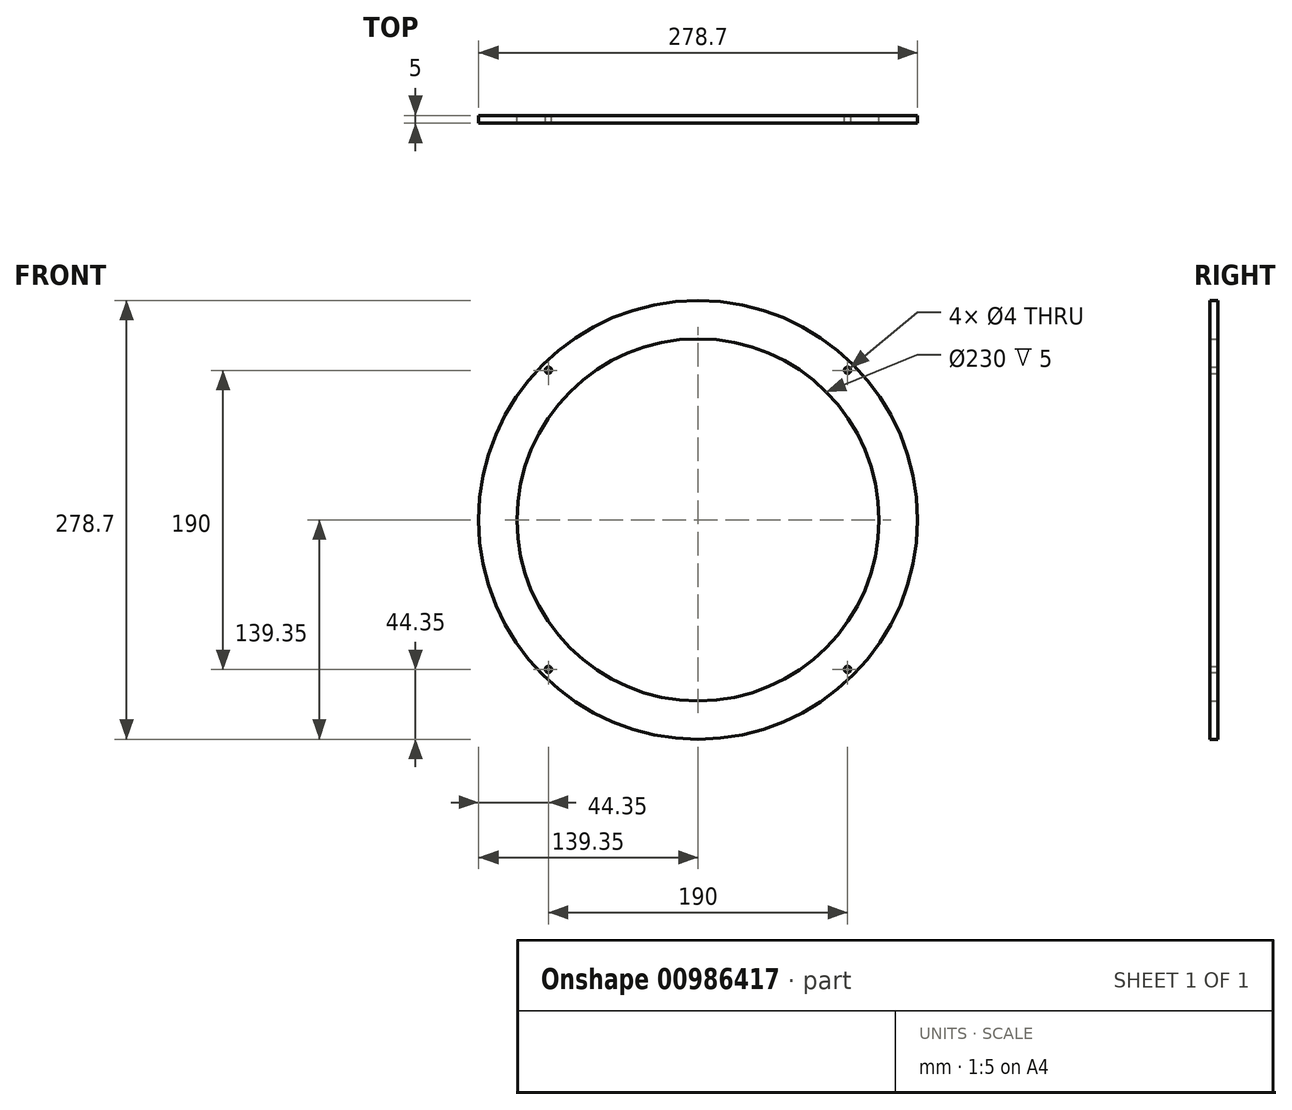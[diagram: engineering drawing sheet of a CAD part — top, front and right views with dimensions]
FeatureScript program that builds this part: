
annotation { "Feature Type Name" : "Feature", "Feature Type Description" : "" }
export const myFeature = defineFeature(function(context is Context, id is Id, definition is map)
    precondition{}
    {
        {
            var Q0;
            Q0=qCreatedBy(makeId("Front.planeOp"),FACE);
            var sketch = newSketch(context, id + "F0", { "sketchPlane" : qUnion([Q0])});
            skCircle(sketch, "E0", {"center": v(0, 0) * mm, "radius": 115 * mm});
            skCircle(sketch, "E1", {"center": v(0, 0) * mm, "radius": 134.35 * mm, "construction": true});
            skLineSegment(sketch, "E2.bottom", {"start": v(95, 95) * mm, "end": v(-95, 95) * mm, "construction": true});
            skLineSegment(sketch, "E2.top", {"start": v(95, -95) * mm, "end": v(-95, -95) * mm, "construction": true});
            skLineSegment(sketch, "E2.left", {"start": v(95, 95) * mm, "end": v(95, -95) * mm, "construction": true});
            skLineSegment(sketch, "E2.right", {"start": v(-95, 95) * mm, "end": v(-95, -95) * mm, "construction": true});
            skCircle(sketch, "E3", {"center": v(95, 95) * mm, "radius": 2 * mm});
            skCircle(sketch, "E4.1.0", {"center": v(-95, 95) * mm, "radius": 2 * mm});
            skCircle(sketch, "E4.2.0", {"center": v(-95, -95) * mm, "radius": 2 * mm});
            skCircle(sketch, "E4.3.0", {"center": v(95, -95) * mm, "radius": 2 * mm});
            skCircle(sketch, "E5", {"center": v(0, 0) * mm, "radius": 139.35 * mm});
            skSolve(sketch);
        }
        {
            var Q0;
            Q0=makeQuery(id+"F0.imprint","IMPRINT",FACE,{"disambiguationData":[TD([[makeQuery(id+"F0.imprint","IMPRINT",EDGE,{"derivedFrom":sQuery(id+"F0.wireOp",EDGE,"E0")}),-1.0]])]});
            extrude(context, id + "F1", {"entities" : qUnion([Q0]), "depth" : 5 * mm, "offsetDistance" : 25 * mm});
        }
    });
